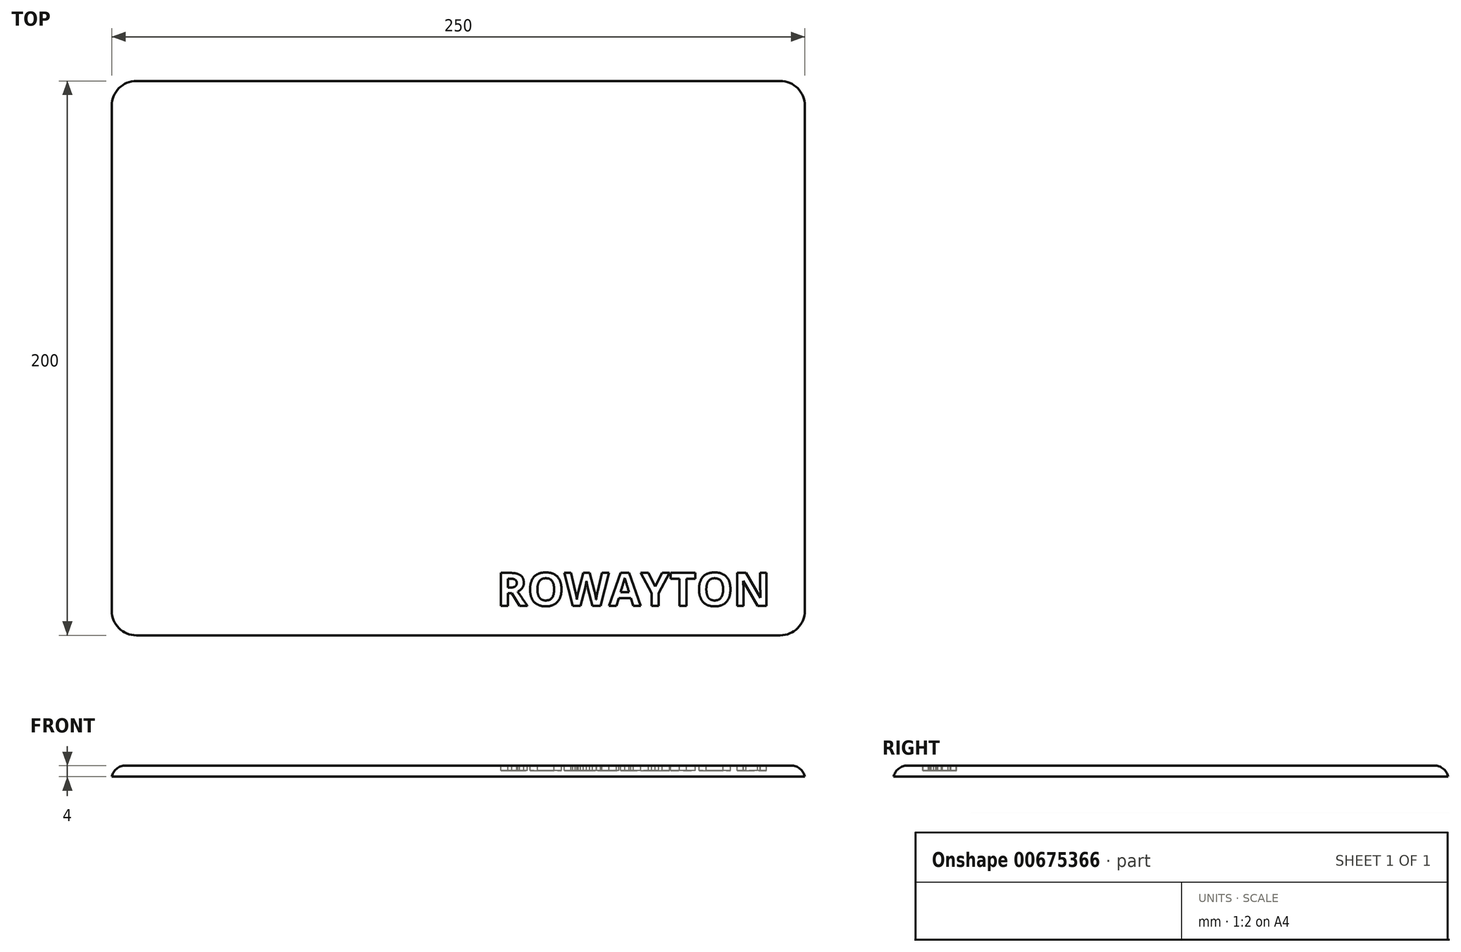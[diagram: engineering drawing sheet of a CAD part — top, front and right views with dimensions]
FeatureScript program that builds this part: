
annotation { "Feature Type Name" : "Feature", "Feature Type Description" : "" }
export const myFeature = defineFeature(function(context is Context, id is Id, definition is map)
    precondition{}
    {
        {
            var Q0;
            Q0=qCreatedBy(makeId("Top.planeOp"),FACE);
            var sketch = newSketch(context, id + "F0", { "sketchPlane" : qUnion([Q0])});
            skLineSegment(sketch, "E0.bottom", {"start": v(125, -100) * mm, "end": v(-125, -100) * mm});
            skLineSegment(sketch, "E0.top", {"start": v(125, 100) * mm, "end": v(-125, 100) * mm});
            skLineSegment(sketch, "E0.left", {"start": v(125, -100) * mm, "end": v(125, 100) * mm});
            skLineSegment(sketch, "E0.right", {"start": v(-125, -100) * mm, "end": v(-125, 100) * mm});
            skPoint(sketch, "E0.middle", {"position": v(0, 0) * mm});
            skSolve(sketch);
        }
        {
            var Q0;
            Q0 = qSketchRegion(id + "F0", true);
            extrude(context, id + "F1", {"entities" : qUnion([Q0]), "depth" : 4 * mm, "offsetDistance" : 25.4 * mm});
        }
        {
            var Q0;
            Q0=makeQuery(id+"F1.opExtrude","SWEPT_EDGE",EDGE,{"disambiguationData":[OSD([sQuery(id+"F0.wireOp",EDGE,"E0.bottom"),sQuery(id+"F0.wireOp",EDGE,"E0.right")])]});
            var Q1;
            Q1=makeQuery(id+"F1.opExtrude","SWEPT_EDGE",EDGE,{"disambiguationData":[OSD([sQuery(id+"F0.wireOp",EDGE,"E0.bottom"),sQuery(id+"F0.wireOp",EDGE,"E0.left")])]});
            var Q2;
            Q2=makeQuery(id+"F1.opExtrude","SWEPT_EDGE",EDGE,{"disambiguationData":[OSD([sQuery(id+"F0.wireOp",EDGE,"E0.top"),sQuery(id+"F0.wireOp",EDGE,"E0.left")])]});
            var Q3;
            Q3=makeQuery(id+"F1.opExtrude","SWEPT_EDGE",EDGE,{"disambiguationData":[OSD([sQuery(id+"F0.wireOp",EDGE,"E0.top"),sQuery(id+"F0.wireOp",EDGE,"E0.right")])]});
            fillet(context, id + "F2", {"entities" : qUnion([Q0, Q1, Q2, Q3]), "radius" : 8.9 * mm, "tangentPropagation" : true, "allowEdgeOverflow" : false});
        }
        {
            var Q0;
            Q0=makeQuery(id+"F1.opExtrude","CAP_EDGE",EDGE,{"disambiguationData":[OSD([sQuery(id+"F0.wireOp",EDGE,"E0.right")])],"isStart":false});
            fillet(context, id + "F3", {"entities" : qUnion([Q0]), "radius" : 5.08 * mm, "tangentPropagation" : true, "allowEdgeOverflow" : false});
        }
        {
            var Q0;
            Q0=makeQuery(id+"F1.opExtrude","CAP_FACE",FACE,{"disambiguationData":[OSD([sQuery(id+"F0.wireOp",EDGE,"E0.bottom"),sQuery(id+"F0.wireOp",EDGE,"E0.top"),sQuery(id+"F0.wireOp",EDGE,"E0.left"),sQuery(id+"F0.wireOp",EDGE,"E0.right")])],"isStart":false});
            var sketch = newSketch(context, id + "F4", { "sketchPlane" : qUnion([Q0])});
            skText(sketch, "E1", { "text": "ROWAYTON", "fontName": "OpenSans-Bold.ttf"});
            const initialGuessF4  = {"E1": [0.01391, -0.08937, 1, 0, 0.012]};
            skSetInitialGuess(sketch, initialGuessF4);
            skSolve(sketch);
        }
        {
            var Q0;
            Q0 = qSketchRegion(id + "F4", true);
            extrude(context, id + "F5", {"entities" : qUnion([Q0]), "operationType" : NewBodyOperationType.REMOVE, "oppositeDirection" : true, "depth" : 1.8 * mm, "offsetDistance" : 25.4 * mm});
        }
    });
